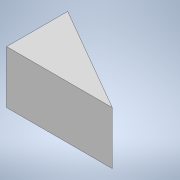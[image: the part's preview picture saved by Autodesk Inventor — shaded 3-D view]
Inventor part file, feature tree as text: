
AUTODESK INVENTOR PART (.ipt)
format: ipt  version: 2020.2 (Build 242310000, 310)  size: 87,552 bytes
history: native  units: in
note: dims shown in document units (in); Inventor stores cm internally (conversion verified against a paired STEP export)
features: extrude x1, sketch x1
ambient origin geometry x8: Origin, YZ Plane, XZ Plane, XY Plane, X Axis, Y Axis, Z Axis, Center Point
bodies: Solid1 (feature_tree)
feature tree (2):
  extrude  "Extrusion1"  TaperAngle=30.0deg  [1 undecoded]
  sketch  "Sketch1"  dims[d0=4.0in d1=30.0deg d2=2.0in d3=0.0in]
note: 1 required parameter value undecoded (feature->parameter linkage not recoverable at this tier; creation-order binding heuristic only, values carry confidence <= 0.55)
